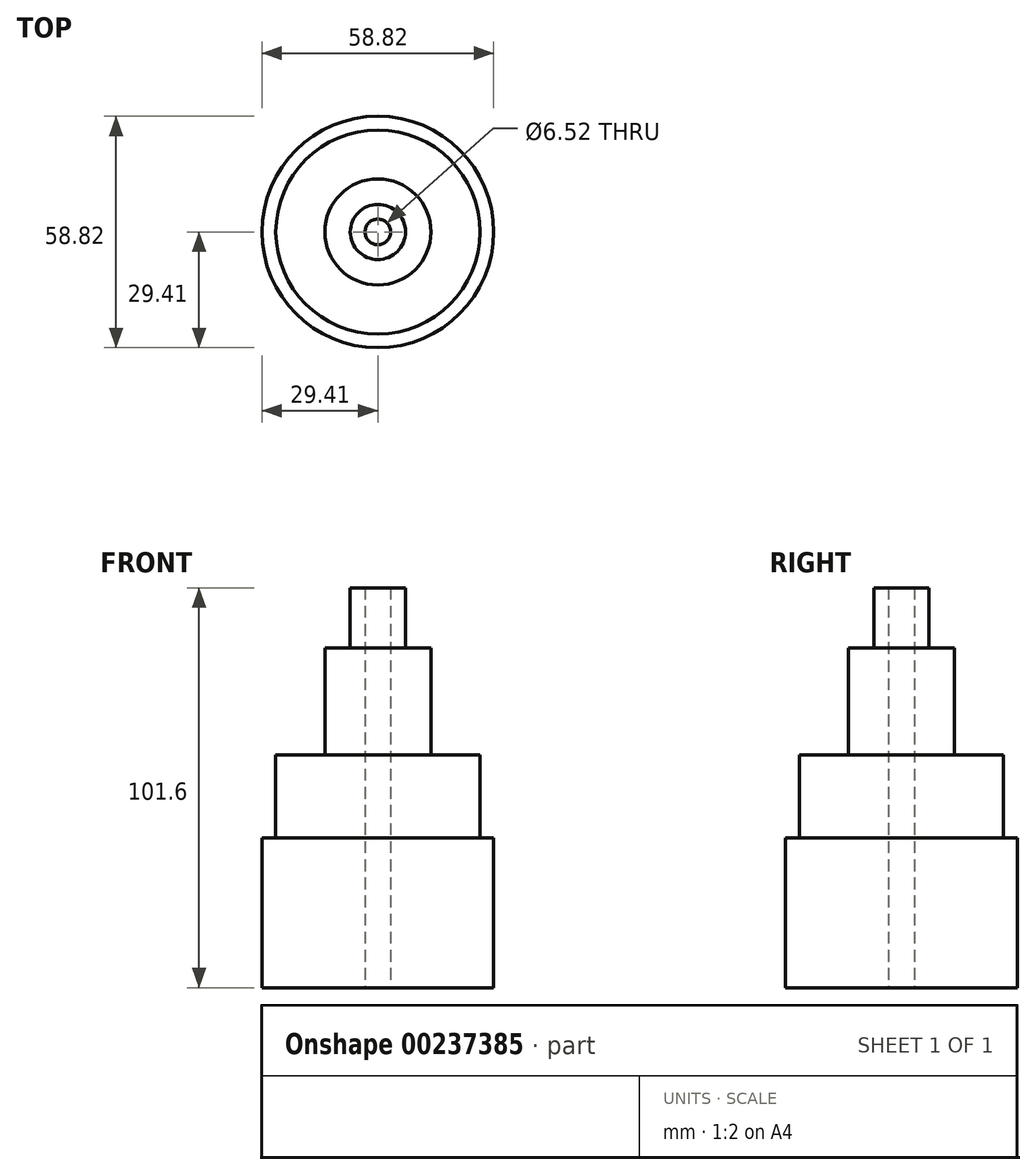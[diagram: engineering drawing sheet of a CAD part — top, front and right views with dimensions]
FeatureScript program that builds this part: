
annotation { "Feature Type Name" : "Feature", "Feature Type Description" : "" }
export const myFeature = defineFeature(function(context is Context, id is Id, definition is map)
    precondition{}
    {
        {
            var Q0;
            Q0=qCreatedBy(makeId("Top.planeOp"),FACE);
            var sketch = newSketch(context, id + "F0", { "sketchPlane" : qUnion([Q0])});
            skCircle(sketch, "E0", {"center": v(0, 0) * mm, "radius": 25.93 * mm});
            skCircle(sketch, "E1", {"center": v(0, 0) * mm, "radius": 13.47 * mm});
            skCircle(sketch, "E2", {"center": v(0, 0) * mm, "radius": 7.01 * mm});
            skCircle(sketch, "E3", {"center": v(0, 0) * mm, "radius": 29.41 * mm});
            skCircle(sketch, "E4", {"center": v(0, 0) * mm, "radius": 3.26 * mm});
            skSolve(sketch);
        }
        {
            var Q0;
            Q0=makeQuery(id+"F0.imprint","IMPRINT",FACE,{"disambiguationData":[TD([[makeQuery(id+"F0.imprint","IMPRINT",EDGE,{"derivedFrom":sQuery(id+"F0.wireOp",EDGE,"E0")}),-1.0]])]});
            extrude(context, id + "F1", {"entities" : qUnion([Q0]), "depth" : 38.1 * mm});
        }
        {
            var Q0;
            Q0=makeQuery(id+"F0.imprint","IMPRINT",FACE,{"disambiguationData":[TD([[makeQuery(id+"F0.imprint","IMPRINT",EDGE,{"derivedFrom":sQuery(id+"F0.wireOp",EDGE,"E0")}),1.0]])]});
            extrude(context, id + "F2", {"entities" : qUnion([Q0]), "operationType" : NewBodyOperationType.ADD, "depth" : 59.18 * mm});
        }
        {
            var Q0;
            Q0=makeQuery(id+"F0.imprint","IMPRINT",FACE,{"disambiguationData":[TD([[makeQuery(id+"F0.imprint","IMPRINT",EDGE,{"derivedFrom":sQuery(id+"F0.wireOp",EDGE,"E1")}),1.0]])]});
            extrude(context, id + "F3", {"entities" : qUnion([Q0]), "operationType" : NewBodyOperationType.ADD, "depth" : 86.36 * mm});
        }
        {
            var Q0;
            Q0=makeQuery(id+"F0.imprint","IMPRINT",FACE,{"disambiguationData":[TD([[makeQuery(id+"F0.imprint","IMPRINT",EDGE,{"derivedFrom":sQuery(id+"F0.wireOp",EDGE,"E1")}),1.0]])]});
            extrude(context, id + "F4", {"entities" : qUnion([Q0]), "operationType" : NewBodyOperationType.ADD, "depth" : 50.8 * mm});
        }
        {
            var Q0;
            Q0=makeQuery(id+"F0.imprint","IMPRINT",FACE,{"disambiguationData":[TD([[makeQuery(id+"F0.imprint","IMPRINT",EDGE,{"derivedFrom":sQuery(id+"F0.wireOp",EDGE,"E2")}),1.0]])]});
            extrude(context, id + "F5", {"entities" : qUnion([Q0]), "operationType" : NewBodyOperationType.ADD, "depth" : 101.6 * mm});
        }
        {
            var Q0;
            Q0=sQuery(id+"F0.wireOp",EDGE,"E4");
            extrude(context, id + "F6", {"bodyType" : ToolBodyType.SURFACE, "surfaceEntities" : qUnion([Q0]), "depth" : 114.3 * mm});
        }
    });
